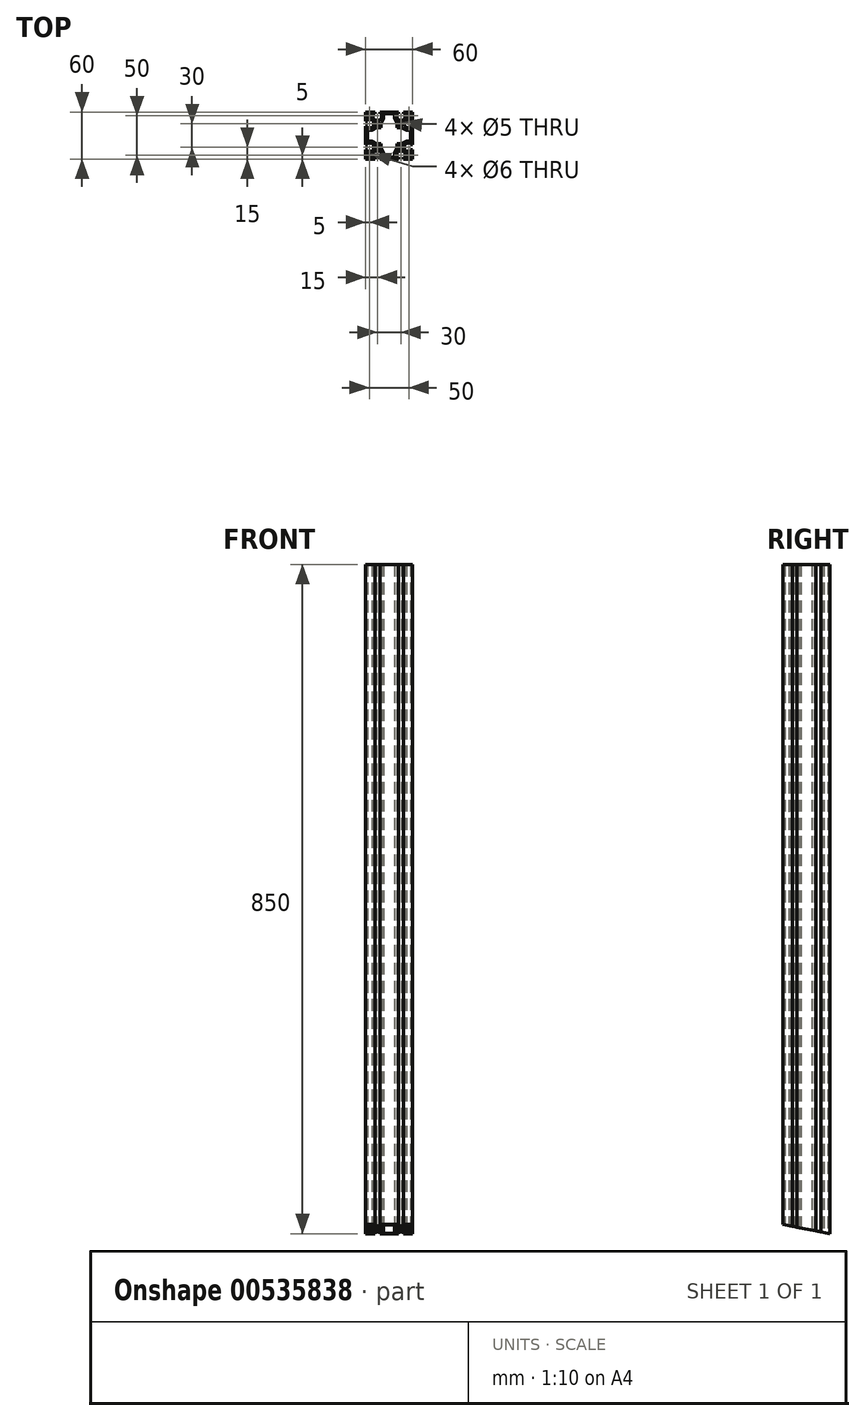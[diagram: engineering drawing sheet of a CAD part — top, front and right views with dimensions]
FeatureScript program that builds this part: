
annotation { "Feature Type Name" : "Feature", "Feature Type Description" : "" }
export const myFeature = defineFeature(function(context is Context, id is Id, definition is map)
    precondition{}
    {
        {
            var Q0;
            Q0=qCreatedBy(makeId("Top.planeOp"),FACE);
            var sketch = newSketch(context, id + "F0", { "sketchPlane" : qUnion([Q0])});
            skLineSegment(sketch, "E0.bottom", {"start": v(30, -30) * mm, "end": v(-30, -30) * mm});
            skLineSegment(sketch, "E0.top", {"start": v(30, 30) * mm, "end": v(-30, 30) * mm});
            skLineSegment(sketch, "E0.left", {"start": v(30, -30) * mm, "end": v(30, 30) * mm});
            skLineSegment(sketch, "E0.right", {"start": v(-30, -30) * mm, "end": v(-30, 30) * mm});
            skPoint(sketch, "E0.middle", {"position": v(0, 0) * mm});
            skLineSegment(sketch, "E1.top", {"start": v(-11.85, 30) * mm, "end": v(-18.15, 30) * mm});
            skLineSegment(sketch, "E1.left", {"start": v(-11.85, 27.5) * mm, "end": v(-11.85, 30) * mm});
            skLineSegment(sketch, "E1.right", {"start": v(-18.15, 27.5) * mm, "end": v(-18.15, 30) * mm});
            skPoint(sketch, "E1.middle", {"position": v(-15, 28.75) * mm});
            skLineSegment(sketch, "E2.bottom", {"start": v(-9.85, 27.5) * mm, "end": v(-11.85, 27.5) * mm});
            skLineSegment(sketch, "E2.left", {"start": v(-9.85, 27.5) * mm, "end": v(-9.85, 21.55) * mm});
            skLineSegment(sketch, "E2.right", {"start": v(-20.15, 27.5) * mm, "end": v(-20.15, 21.55) * mm});
            skPoint(sketch, "E2.middle", {"position": v(-15, 24.52) * mm});
            skArc(sketch, "E3", {"start": v(-20.15, 21.55) * mm, "mid": v(-15, 19.5) * mm, "end": v(-9.85, 21.55) * mm});
            skPoint(sketch, "E4.MirrorP", {"position": v(15, 24.52) * mm});
            skPoint(sketch, "E5.MirrorP", {"position": v(15, 28.75) * mm});
            skLineSegment(sketch, "E6.MirrorCS", {"start": v(11.85, 27.5) * mm, "end": v(11.85, 30) * mm});
            skLineSegment(sketch, "E7.MirrorCS", {"start": v(18.15, 27.5) * mm, "end": v(18.15, 30) * mm});
            skLineSegment(sketch, "E8.MirrorCS", {"start": v(9.85, 27.5) * mm, "end": v(11.85, 27.5) * mm});
            skLineSegment(sketch, "E9.MirrorCS", {"start": v(9.85, 27.5) * mm, "end": v(9.85, 21.55) * mm});
            skArc(sketch, "E10.MirrorCS", {"start": v(20.15, 21.55) * mm, "mid": v(15, 19.5) * mm, "end": v(9.85, 21.55) * mm});
            skLineSegment(sketch, "E11.MirrorCS", {"start": v(20.15, 27.5) * mm, "end": v(20.15, 21.55) * mm});
            skLineSegment(sketch, "E12.MirrorCS", {"start": v(11.85, 30) * mm, "end": v(18.15, 30) * mm});
            skLineSegment(sketch, "E13.1.0", {"start": v(27.5, 20.15) * mm, "end": v(21.55, 20.15) * mm});
            skLineSegment(sketch, "E13.1.1", {"start": v(27.5, 9.85) * mm, "end": v(21.55, 9.85) * mm});
            skArc(sketch, "E13.1.2", {"start": v(21.55, 20.15) * mm, "mid": v(19.5, 15) * mm, "end": v(21.55, 9.85) * mm});
            skLineSegment(sketch, "E13.1.3", {"start": v(27.5, -9.85) * mm, "end": v(21.55, -9.85) * mm});
            skLineSegment(sketch, "E13.1.4", {"start": v(27.5, -20.15) * mm, "end": v(21.55, -20.15) * mm});
            skPoint(sketch, "E13.1.5", {"position": v(28.75, 15) * mm});
            skPoint(sketch, "E13.1.6", {"position": v(28.75, -15) * mm});
            skArc(sketch, "E13.1.7", {"start": v(21.55, -20.15) * mm, "mid": v(19.5, -15) * mm, "end": v(21.55, -9.85) * mm});
            skPoint(sketch, "E13.1.8", {"position": v(24.52, -15) * mm});
            skPoint(sketch, "E13.1.9", {"position": v(24.52, 15) * mm});
            skLineSegment(sketch, "E13.1.10", {"start": v(27.5, 9.85) * mm, "end": v(27.5, 20.15) * mm});
            skLineSegment(sketch, "E13.1.11", {"start": v(27.5, -11.85) * mm, "end": v(27.5, -18.15) * mm});
            skLineSegment(sketch, "E13.1.12", {"start": v(30, 11.85) * mm, "end": v(30, 18.15) * mm});
            skLineSegment(sketch, "E13.1.13", {"start": v(30, -11.85) * mm, "end": v(30, -18.15) * mm});
            skLineSegment(sketch, "E13.1.14", {"start": v(27.5, 18.15) * mm, "end": v(30, 18.15) * mm});
            skLineSegment(sketch, "E13.1.15", {"start": v(27.5, 11.85) * mm, "end": v(30, 11.85) * mm});
            skLineSegment(sketch, "E13.1.16", {"start": v(27.5, 11.85) * mm, "end": v(27.5, 18.15) * mm});
            skLineSegment(sketch, "E13.1.17", {"start": v(27.5, -9.85) * mm, "end": v(27.5, -20.15) * mm});
            skLineSegment(sketch, "E13.1.18", {"start": v(27.5, -18.15) * mm, "end": v(30, -18.15) * mm});
            skLineSegment(sketch, "E13.1.19", {"start": v(27.5, -11.85) * mm, "end": v(30, -11.85) * mm});
            skLineSegment(sketch, "E13.2.0", {"start": v(20.15, -27.5) * mm, "end": v(20.15, -21.55) * mm});
            skLineSegment(sketch, "E13.2.1", {"start": v(9.85, -27.5) * mm, "end": v(9.85, -21.55) * mm});
            skArc(sketch, "E13.2.2", {"start": v(20.15, -21.55) * mm, "mid": v(15, -19.5) * mm, "end": v(9.85, -21.55) * mm});
            skLineSegment(sketch, "E13.2.3", {"start": v(-9.85, -27.5) * mm, "end": v(-9.85, -21.55) * mm});
            skLineSegment(sketch, "E13.2.4", {"start": v(-20.15, -27.5) * mm, "end": v(-20.15, -21.55) * mm});
            skPoint(sketch, "E13.2.5", {"position": v(15, -28.75) * mm});
            skPoint(sketch, "E13.2.6", {"position": v(-15, -28.75) * mm});
            skArc(sketch, "E13.2.7", {"start": v(-20.15, -21.55) * mm, "mid": v(-15, -19.5) * mm, "end": v(-9.85, -21.55) * mm});
            skPoint(sketch, "E13.2.8", {"position": v(-15, -24.52) * mm});
            skPoint(sketch, "E13.2.9", {"position": v(15, -24.52) * mm});
            skLineSegment(sketch, "E13.2.10", {"start": v(9.85, -27.5) * mm, "end": v(20.15, -27.5) * mm});
            skLineSegment(sketch, "E13.2.11", {"start": v(-11.85, -27.5) * mm, "end": v(-18.15, -27.5) * mm});
            skLineSegment(sketch, "E13.2.12", {"start": v(11.85, -30) * mm, "end": v(18.15, -30) * mm});
            skLineSegment(sketch, "E13.2.13", {"start": v(-11.85, -30) * mm, "end": v(-18.15, -30) * mm});
            skLineSegment(sketch, "E13.2.14", {"start": v(18.15, -27.5) * mm, "end": v(18.15, -30) * mm});
            skLineSegment(sketch, "E13.2.15", {"start": v(11.85, -27.5) * mm, "end": v(11.85, -30) * mm});
            skLineSegment(sketch, "E13.2.16", {"start": v(11.85, -27.5) * mm, "end": v(18.15, -27.5) * mm});
            skLineSegment(sketch, "E13.2.17", {"start": v(-9.85, -27.5) * mm, "end": v(-20.15, -27.5) * mm});
            skLineSegment(sketch, "E13.2.18", {"start": v(-18.15, -27.5) * mm, "end": v(-18.15, -30) * mm});
            skLineSegment(sketch, "E13.2.19", {"start": v(-11.85, -27.5) * mm, "end": v(-11.85, -30) * mm});
            skLineSegment(sketch, "E13.3.0", {"start": v(-27.5, -20.15) * mm, "end": v(-21.55, -20.15) * mm});
            skLineSegment(sketch, "E13.3.1", {"start": v(-27.5, -9.85) * mm, "end": v(-21.55, -9.85) * mm});
            skArc(sketch, "E13.3.2", {"start": v(-21.55, -20.15) * mm, "mid": v(-19.5, -15) * mm, "end": v(-21.55, -9.85) * mm});
            skLineSegment(sketch, "E13.3.3", {"start": v(-27.5, 9.85) * mm, "end": v(-21.55, 9.85) * mm});
            skLineSegment(sketch, "E13.3.4", {"start": v(-27.5, 20.15) * mm, "end": v(-21.55, 20.15) * mm});
            skPoint(sketch, "E13.3.5", {"position": v(-28.75, -15) * mm});
            skPoint(sketch, "E13.3.6", {"position": v(-28.75, 15) * mm});
            skArc(sketch, "E13.3.7", {"start": v(-21.55, 20.15) * mm, "mid": v(-19.5, 15) * mm, "end": v(-21.55, 9.85) * mm});
            skPoint(sketch, "E13.3.8", {"position": v(-24.52, 15) * mm});
            skPoint(sketch, "E13.3.9", {"position": v(-24.52, -15) * mm});
            skLineSegment(sketch, "E13.3.10", {"start": v(-27.5, -9.85) * mm, "end": v(-27.5, -20.15) * mm});
            skLineSegment(sketch, "E13.3.11", {"start": v(-27.5, 11.85) * mm, "end": v(-27.5, 18.15) * mm});
            skLineSegment(sketch, "E13.3.12", {"start": v(-30, -11.85) * mm, "end": v(-30, -18.15) * mm});
            skLineSegment(sketch, "E13.3.13", {"start": v(-30, 11.85) * mm, "end": v(-30, 18.15) * mm});
            skLineSegment(sketch, "E13.3.14", {"start": v(-27.5, -18.15) * mm, "end": v(-30, -18.15) * mm});
            skLineSegment(sketch, "E13.3.15", {"start": v(-27.5, -11.85) * mm, "end": v(-30, -11.85) * mm});
            skLineSegment(sketch, "E13.3.16", {"start": v(-27.5, -11.85) * mm, "end": v(-27.5, -18.15) * mm});
            skLineSegment(sketch, "E13.3.17", {"start": v(-27.5, 9.85) * mm, "end": v(-27.5, 20.15) * mm});
            skLineSegment(sketch, "E13.3.18", {"start": v(-27.5, 18.15) * mm, "end": v(-30, 18.15) * mm});
            skLineSegment(sketch, "E13.3.19", {"start": v(-27.5, 11.85) * mm, "end": v(-30, 11.85) * mm});
            skLineSegment(sketch, "E13.anchor1", {"start": v(0, 0) * mm, "end": v(-20.15, 21.55) * mm, "construction": true});
            skLineSegment(sketch, "E13.anchor2", {"start": v(0, 0) * mm, "end": v(-21.55, -20.15) * mm, "construction": true});
            skLineSegment(sketch, "E14.trimOffspring", {"start": v(-18.15, 27.5) * mm, "end": v(-20.15, 27.5) * mm});
            skLineSegment(sketch, "E15.trimOffspring", {"start": v(18.15, 27.5) * mm, "end": v(20.15, 27.5) * mm});
            skCircle(sketch, "E16", {"center": v(-15, 15) * mm, "radius": 2.5 * mm});
            skCircle(sketch, "E17", {"center": v(-25, 25) * mm, "radius": 3 * mm});
            skCircle(sketch, "E18.MirrorC", {"center": v(25, 25) * mm, "radius": 3 * mm});
            skCircle(sketch, "E19.MirrorC", {"center": v(25, -25) * mm, "radius": 3 * mm});
            skCircle(sketch, "E20.MirrorC", {"center": v(-25, -25) * mm, "radius": 3 * mm});
            skCircle(sketch, "E21.MirrorC", {"center": v(15, 15) * mm, "radius": 2.5 * mm});
            skCircle(sketch, "E22.MirrorC", {"center": v(15, -15) * mm, "radius": 2.5 * mm});
            skCircle(sketch, "E23.MirrorC", {"center": v(-15, -15) * mm, "radius": 2.5 * mm});
            skLineSegment(sketch, "E24", {"start": v(-7, 27.5) * mm, "end": v(0, 27.5) * mm});
            skLineSegment(sketch, "E25", {"start": v(-7, 27.5) * mm, "end": v(-7, 22) * mm});
            skLineSegment(sketch, "E26", {"start": v(-10, 10) * mm, "end": v(-10, 16) * mm});
            skLineSegment(sketch, "E27", {"start": v(-10, 16) * mm, "end": v(-7, 22) * mm});
            skLineSegment(sketch, "E28.MirrorCS", {"start": v(10, 10) * mm, "end": v(10, 16) * mm});
            skLineSegment(sketch, "E29.MirrorCS", {"start": v(10, 16) * mm, "end": v(7, 22) * mm});
            skLineSegment(sketch, "E30.MirrorCS", {"start": v(7, 27.5) * mm, "end": v(0, 27.5) * mm});
            skLineSegment(sketch, "E31.MirrorCS", {"start": v(7, 27.5) * mm, "end": v(7, 22) * mm});
            skLineSegment(sketch, "E32.1.0", {"start": v(-10, -10) * mm, "end": v(-16, -10) * mm});
            skLineSegment(sketch, "E32.1.1", {"start": v(-16, -10) * mm, "end": v(-22, -7) * mm});
            skLineSegment(sketch, "E32.1.2", {"start": v(-27.5, -7) * mm, "end": v(-22, -7) * mm});
            skLineSegment(sketch, "E32.1.3", {"start": v(-27.5, -7) * mm, "end": v(-27.5, 0) * mm});
            skLineSegment(sketch, "E32.1.4", {"start": v(-27.5, 7) * mm, "end": v(-27.5, 0) * mm});
            skLineSegment(sketch, "E32.1.5", {"start": v(-27.5, 7) * mm, "end": v(-22, 7) * mm});
            skLineSegment(sketch, "E32.1.6", {"start": v(-16, 10) * mm, "end": v(-22, 7) * mm});
            skLineSegment(sketch, "E32.1.7", {"start": v(-10, 10) * mm, "end": v(-16, 10) * mm});
            skLineSegment(sketch, "E32.2.0", {"start": v(10, -10) * mm, "end": v(10, -16) * mm});
            skLineSegment(sketch, "E32.2.1", {"start": v(10, -16) * mm, "end": v(7, -22) * mm});
            skLineSegment(sketch, "E32.2.2", {"start": v(7, -27.5) * mm, "end": v(7, -22) * mm});
            skLineSegment(sketch, "E32.2.3", {"start": v(7, -27.5) * mm, "end": v(0, -27.5) * mm});
            skLineSegment(sketch, "E32.2.4", {"start": v(-7, -27.5) * mm, "end": v(0, -27.5) * mm});
            skLineSegment(sketch, "E32.2.5", {"start": v(-7, -27.5) * mm, "end": v(-7, -22) * mm});
            skLineSegment(sketch, "E32.2.6", {"start": v(-10, -16) * mm, "end": v(-7, -22) * mm});
            skLineSegment(sketch, "E32.2.7", {"start": v(-10, -10) * mm, "end": v(-10, -16) * mm});
            skLineSegment(sketch, "E32.3.0", {"start": v(10, 10) * mm, "end": v(16, 10) * mm});
            skLineSegment(sketch, "E32.3.1", {"start": v(16, 10) * mm, "end": v(22, 7) * mm});
            skLineSegment(sketch, "E32.3.2", {"start": v(27.5, 7) * mm, "end": v(22, 7) * mm});
            skLineSegment(sketch, "E32.3.3", {"start": v(27.5, 7) * mm, "end": v(27.5, 0) * mm});
            skLineSegment(sketch, "E32.3.4", {"start": v(27.5, -7) * mm, "end": v(27.5, 0) * mm});
            skLineSegment(sketch, "E32.3.5", {"start": v(27.5, -7) * mm, "end": v(22, -7) * mm});
            skLineSegment(sketch, "E32.3.6", {"start": v(16, -10) * mm, "end": v(22, -7) * mm});
            skLineSegment(sketch, "E32.3.7", {"start": v(10, -10) * mm, "end": v(16, -10) * mm});
            skSolve(sketch);
        }
        {
            var Q0;
            {var subQ30=sQuery(id+"F0.wireOp",EDGE,"E1.left");Q0=makeQuery(id+"F0.imprint","IMPRINT",FACE,{"disambiguationData":[TD([[makeQuery(id+"F0.imprint","IMPRINT",EDGE,{"derivedFrom":subQ30}),-1.0]])]});}
            extrude(context, id + "F1", {"entities" : qUnion([Q0]), "depth" : 850 * mm, "offsetDistance" : 25 * mm});
        }
        {
            var Q0;
            Q0=makeQuery(id+"F1.opExtrude","SWEPT_EDGE",EDGE,{"disambiguationData":[OSD([sQuery(id+"F0.wireOp",EDGE,"E24"),sQuery(id+"F0.wireOp",EDGE,"E25")])]});
            var Q1;
            Q1=makeQuery(id+"F1.opExtrude","SWEPT_EDGE",EDGE,{"disambiguationData":[OSD([sQuery(id+"F0.wireOp",EDGE,"E30.MirrorCS"),sQuery(id+"F0.wireOp",EDGE,"E31.MirrorCS")])]});
            var Q2;
            Q2=makeQuery(id+"F1.opExtrude","SWEPT_EDGE",EDGE,{"disambiguationData":[OSD([sQuery(id+"F0.wireOp",EDGE,"840db5bc-c403-45cd-90c7-254e62d9e8c5.3.2"),sQuery(id+"F0.wireOp",EDGE,"840db5bc-c403-45cd-90c7-254e62d9e8c5.3.3")])]});
            var Q3;
            Q3=makeQuery(id+"F1.opExtrude","SWEPT_EDGE",EDGE,{"disambiguationData":[OSD([sQuery(id+"F0.wireOp",EDGE,"840db5bc-c403-45cd-90c7-254e62d9e8c5.3.4"),sQuery(id+"F0.wireOp",EDGE,"840db5bc-c403-45cd-90c7-254e62d9e8c5.3.5")])]});
            var Q4;
            Q4=makeQuery(id+"F1.opExtrude","SWEPT_EDGE",EDGE,{"disambiguationData":[OSD([sQuery(id+"F0.wireOp",EDGE,"840db5bc-c403-45cd-90c7-254e62d9e8c5.1.4"),sQuery(id+"F0.wireOp",EDGE,"840db5bc-c403-45cd-90c7-254e62d9e8c5.1.5")])]});
            var Q5;
            Q5=makeQuery(id+"F1.opExtrude","SWEPT_EDGE",EDGE,{"disambiguationData":[OSD([sQuery(id+"F0.wireOp",EDGE,"840db5bc-c403-45cd-90c7-254e62d9e8c5.1.2"),sQuery(id+"F0.wireOp",EDGE,"840db5bc-c403-45cd-90c7-254e62d9e8c5.1.3")])]});
            var Q6;
            Q6=makeQuery(id+"F1.opExtrude","SWEPT_EDGE",EDGE,{"disambiguationData":[OSD([sQuery(id+"F0.wireOp",EDGE,"840db5bc-c403-45cd-90c7-254e62d9e8c5.2.2"),sQuery(id+"F0.wireOp",EDGE,"840db5bc-c403-45cd-90c7-254e62d9e8c5.2.3")])]});
            var Q7;
            Q7=makeQuery(id+"F1.opExtrude","SWEPT_EDGE",EDGE,{"disambiguationData":[OSD([sQuery(id+"F0.wireOp",EDGE,"840db5bc-c403-45cd-90c7-254e62d9e8c5.2.4"),sQuery(id+"F0.wireOp",EDGE,"840db5bc-c403-45cd-90c7-254e62d9e8c5.2.5")])]});
            fillet(context, id + "F2", {"entities" : qUnion([Q0, Q1, Q2, Q3, Q4, Q5, Q6, Q7]), "radius" : 2 * mm, "tangentPropagation" : true, "allowEdgeOverflow" : false});
        }
        {
            var Q0;
            Q0=makeQuery(id+"F1.opExtrude","SWEPT_EDGE",EDGE,{"disambiguationData":[OSD([sQuery(id+"F0.wireOp",EDGE,"E26"),sQuery(id+"F0.wireOp",EDGE,"E27")])]});
            var Q1;
            Q1=makeQuery(id+"F1.opExtrude","SWEPT_EDGE",EDGE,{"disambiguationData":[OSD([sQuery(id+"F0.wireOp",EDGE,"E28.MirrorCS"),sQuery(id+"F0.wireOp",EDGE,"E29.MirrorCS")])]});
            var Q2;
            Q2=makeQuery(id+"F1.opExtrude","SWEPT_EDGE",EDGE,{"disambiguationData":[OSD([sQuery(id+"F0.wireOp",EDGE,"840db5bc-c403-45cd-90c7-254e62d9e8c5.3.0"),sQuery(id+"F0.wireOp",EDGE,"840db5bc-c403-45cd-90c7-254e62d9e8c5.3.1")])]});
            var Q3;
            Q3=makeQuery(id+"F1.opExtrude","SWEPT_EDGE",EDGE,{"disambiguationData":[OSD([sQuery(id+"F0.wireOp",EDGE,"840db5bc-c403-45cd-90c7-254e62d9e8c5.1.6"),sQuery(id+"F0.wireOp",EDGE,"840db5bc-c403-45cd-90c7-254e62d9e8c5.1.7")])]});
            var Q4;
            Q4=makeQuery(id+"F1.opExtrude","SWEPT_EDGE",EDGE,{"disambiguationData":[OSD([sQuery(id+"F0.wireOp",EDGE,"840db5bc-c403-45cd-90c7-254e62d9e8c5.1.0"),sQuery(id+"F0.wireOp",EDGE,"840db5bc-c403-45cd-90c7-254e62d9e8c5.1.1")])]});
            var Q5;
            Q5=makeQuery(id+"F1.opExtrude","SWEPT_EDGE",EDGE,{"disambiguationData":[OSD([sQuery(id+"F0.wireOp",EDGE,"840db5bc-c403-45cd-90c7-254e62d9e8c5.3.6"),sQuery(id+"F0.wireOp",EDGE,"840db5bc-c403-45cd-90c7-254e62d9e8c5.3.7")])]});
            var Q6;
            Q6=makeQuery(id+"F1.opExtrude","SWEPT_EDGE",EDGE,{"disambiguationData":[OSD([sQuery(id+"F0.wireOp",EDGE,"840db5bc-c403-45cd-90c7-254e62d9e8c5.2.0"),sQuery(id+"F0.wireOp",EDGE,"840db5bc-c403-45cd-90c7-254e62d9e8c5.2.1")])]});
            var Q7;
            Q7=makeQuery(id+"F1.opExtrude","SWEPT_EDGE",EDGE,{"disambiguationData":[OSD([sQuery(id+"F0.wireOp",EDGE,"840db5bc-c403-45cd-90c7-254e62d9e8c5.2.6"),sQuery(id+"F0.wireOp",EDGE,"840db5bc-c403-45cd-90c7-254e62d9e8c5.2.7")])]});
            fillet(context, id + "F3", {"entities" : qUnion([Q0, Q1, Q2, Q3, Q4, Q5, Q6, Q7]), "radius" : 7 * mm, "tangentPropagation" : true, "allowEdgeOverflow" : false});
        }
        {
            var Q0;
            Q0=qCreatedBy(makeId("Right.planeOp"),FACE);
            var sketch = newSketch(context, id + "F4", { "sketchPlane" : qUnion([Q0])});
            skLineSegment(sketch, "E33.MirrorCS", {"start": v(-188.6, -83.55) * mm, "end": v(5.7, -122.2) * mm});
            skLineSegment(sketch, "E34.MirrorCS", {"start": v(-164.29, 38.65) * mm, "end": v(30, 0) * mm});
            skLineSegment(sketch, "E35.MirrorCS", {"start": v(-164.29, 38.65) * mm, "end": v(-188.6, -83.55) * mm});
            skLineSegment(sketch, "E36.MirrorCS", {"start": v(30, 0) * mm, "end": v(5.7, -122.2) * mm});
            skSolve(sketch);
        }
        {
            var Q0;
            Q0 = qSketchRegion(id + "F4", true);
            extrude(context, id + "F5", {"entities" : qUnion([Q0]), "operationType" : NewBodyOperationType.REMOVE, "depth" : 30 * mm, "offsetDistance" : 25 * mm, "hasSecondDirection" : true, "secondDirectionOppositeDirection" : true, "secondDirectionDepth" : 30 * mm});
        }
    });
